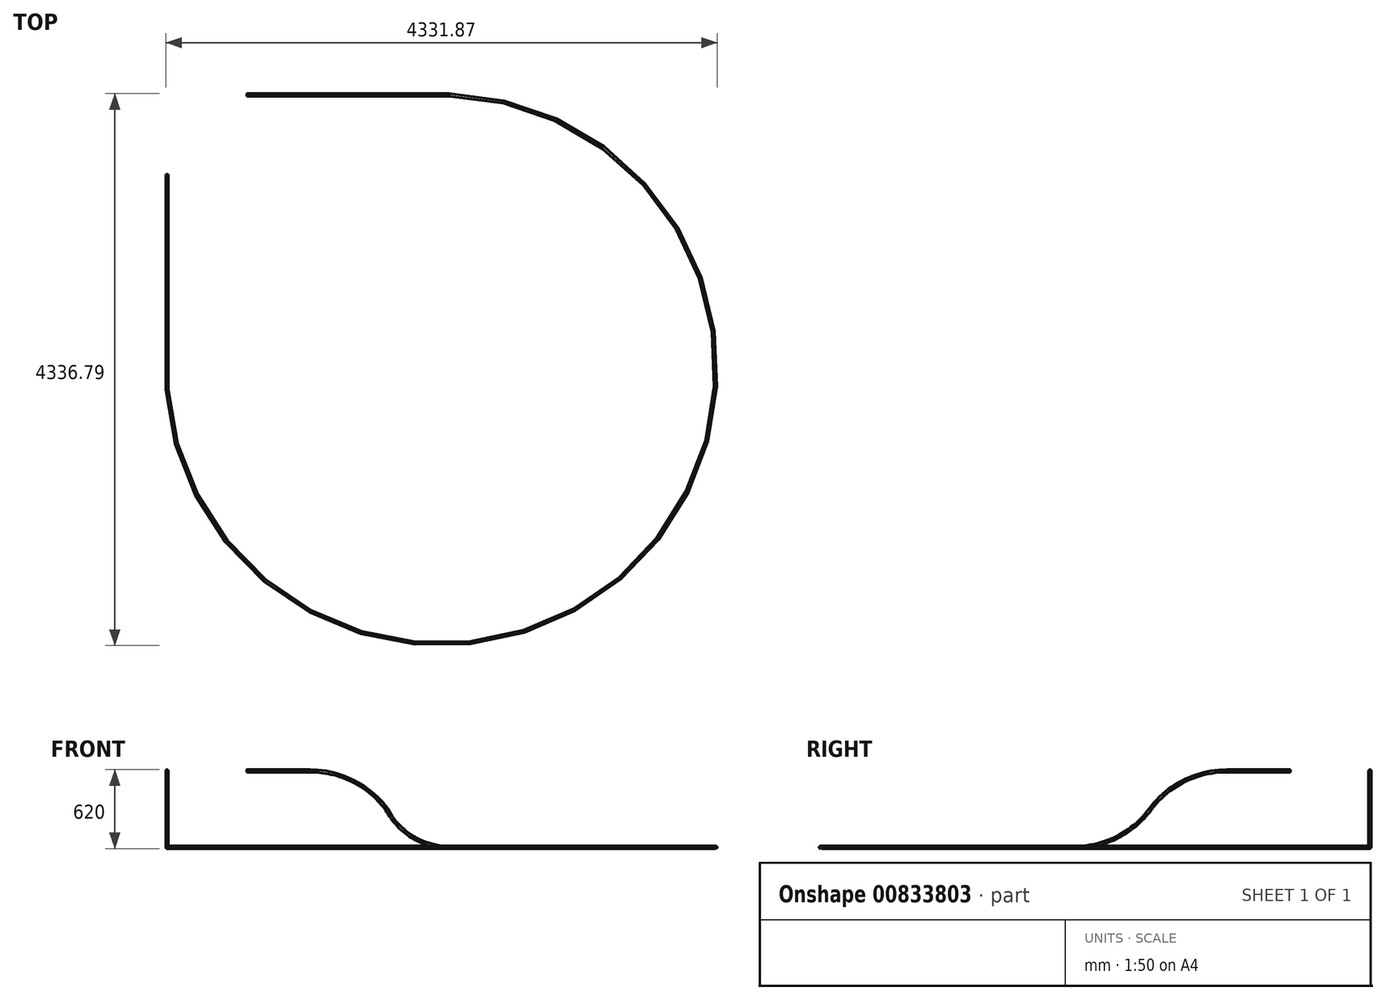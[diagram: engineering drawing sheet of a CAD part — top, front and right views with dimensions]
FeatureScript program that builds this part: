
annotation { "Feature Type Name" : "Feature", "Feature Type Description" : "" }
export const myFeature = defineFeature(function(context is Context, id is Id, definition is map)
    precondition{}
    {
        {
            var Q0;
            Q0=qCreatedBy(makeId("Top.planeOp"),FACE);
            var sketch = newSketch(context, id + "F0", { "sketchPlane" : qUnion([Q0])});
            skLineSegment(sketch, "E0", {"start": v(0, 0) * mm, "end": v(0, 1250) * mm});
            skLineSegment(sketch, "E1", {"start": v(0, 1250) * mm, "end": v(-1250, 1250) * mm});
            skLineSegment(sketch, "E2", {"start": v(-1250, 1250) * mm, "end": v(-1250, 0) * mm});
            skLineSegment(sketch, "E3", {"start": v(-1250, 0) * mm, "end": v(0, 0) * mm});
            skPoint(sketch, "E4", {"position": v(0, 625) * mm});
            skPoint(sketch, "E5", {"position": v(-625, 0) * mm});
            skSolve(sketch);
        }
        {
            var Q0;
            Q0=sQuery(id+"F0.wireOp",VERTEX,"E4");
            var Q1;
            Q1=sQuery(id+"F0.wireOp",EDGE,"E0");
            cPlane(context, id + "F1", {"entities" : qUnion([Q0, Q1]), "cplaneType" : CPlaneType.LINE_POINT, "offset" : 25 * mm, "width" : 150 * mm, "height" : 150 * mm});
        }
        {
            var Q0;
            Q0=qCreatedBy(id+"F1.planeOp",FACE);
            var sketch = newSketch(context, id + "F2", { "sketchPlane" : qUnion([Q0])});
            skLineSegment(sketch, "E6", {"start": v(0, 0) * mm, "end": v(-500, 0) * mm});
            skLineSegment(sketch, "E7", {"start": v(-500, 0) * mm, "end": v(-500, -300) * mm});
            skLineSegment(sketch, "E8", {"start": v(-500, -300) * mm, "end": v(-1100, -300) * mm});
            skArc(sketch, "E9", {"start": v(-500, 0) * mm, "mid": v(-835.41, -79.18) * mm, "end": v(-1100, -300) * mm});
            skLineSegment(sketch, "E10", {"start": v(-1100, -300) * mm, "end": v(-1100, -600) * mm});
            skLineSegment(sketch, "E11", {"start": v(-1100, -600) * mm, "end": v(-1591.48, -600) * mm});
            skArc(sketch, "E12", {"start": v(-1591.48, -600) * mm, "mid": v(-1303.57, -519.07) * mm, "end": v(-1100, -300) * mm});
            skLineSegment(sketch, "E13", {"start": v(-1591.48, -600) * mm, "end": v(-1591.48, -479.86) * mm});
            skSolve(sketch);
        }
        {
            var Q0;
            Q0=sQuery(id+"F0.wireOp",EDGE,"E3");
            cPoint(context, id + "F3", {"entities" : qUnion([Q0]), "parameter" : 0.5});
        }
        {
            var Q0;
            Q0 = qCreatedBy(id + "F3" ,VERTEX);
            var Q1;
            Q1=sQuery(id+"F0.wireOp",EDGE,"E3");
            cPlane(context, id + "F4", {"entities" : qUnion([Q0, Q1]), "cplaneType" : CPlaneType.LINE_POINT, "offset" : 25 * mm, "width" : 150 * mm, "height" : 150 * mm});
        }
        {
            var Q0;
            Q0=qCreatedBy(id+"F4.planeOp",FACE);
            var sketch = newSketch(context, id + "F5", { "sketchPlane" : qUnion([Q0])});
            skLineSegment(sketch, "E14", {"start": v(0, 0) * mm, "end": v(-500, 0) * mm});
            skLineSegment(sketch, "E15", {"start": v(-500, 0) * mm, "end": v(-500, -300) * mm});
            skLineSegment(sketch, "E16", {"start": v(-500, -300) * mm, "end": v(-1100, -300) * mm});
            skLineSegment(sketch, "E17", {"start": v(-1100, -300) * mm, "end": v(-1100, -600) * mm});
            skLineSegment(sketch, "E18", {"start": v(-1100, -600) * mm, "end": v(-1691.38, -600) * mm});
            skArc(sketch, "E19", {"start": v(-500, 0) * mm, "mid": v(-835.41, -79.18) * mm, "end": v(-1100, -300) * mm});
            skArc(sketch, "E20", {"start": v(-1691.38, -600) * mm, "mid": v(-1359.82, -520.71) * mm, "end": v(-1100, -300) * mm});
            skSolve(sketch);
        }
        {
            var Q0;
            Q0=sQuery(id+"F2.wireOp",VERTEX,"E11.end");
            var Q1;
            Q1=sQuery(id+"F2.wireOp",EDGE,"E13");
            cPlane(context, id + "F6", {"entities" : qUnion([Q0, Q1]), "cplaneType" : CPlaneType.LINE_POINT, "offset" : 25 * mm, "width" : 150 * mm, "height" : 150 * mm});
        }
        {
            var Q0;
            Q0=qCreatedBy(id+"F6.planeOp",FACE);
            var sketch = newSketch(context, id + "F7", { "sketchPlane" : qUnion([Q0])});
            skArc(sketch, "E21", {"start": v(-624.99, -1691.37) * mm, "mid": v(3087.67, -3025.27) * mm, "end": v(1591.48, 625) * mm});
            skSolve(sketch);
        }
        {
            var Q0;
            Q0=sQuery(id+"F0.wireOp",EDGE,"E0");
            cPoint(context, id + "F8", {"entities" : qUnion([Q0]), "parameter" : 0.5});
        }
        {
            var Q0;
            Q0 = qCreatedBy(id + "F8" ,VERTEX);
            var Q1;
            Q1=sQuery(id+"F2.wireOp",EDGE,"E6");
            cPlane(context, id + "F9", {"entities" : qUnion([Q0, Q1]), "cplaneType" : CPlaneType.LINE_POINT, "offset" : 25 * mm, "width" : 150 * mm, "height" : 150 * mm});
        }
        {
            var Q0;
            Q0=sQuery(id+"F0.wireOp",VERTEX,"E5");
            var Q1;
            Q1=sQuery(id+"F5.wireOp",EDGE,"E14");
            cPlane(context, id + "F10", {"entities" : qUnion([Q0, Q1]), "cplaneType" : CPlaneType.LINE_POINT, "offset" : 25 * mm, "width" : 150 * mm, "height" : 150 * mm});
        }
        {
            var Q0;
            Q0=qCreatedBy(id+"F10.planeOp",FACE);
            var sketch = newSketch(context, id + "F11", { "sketchPlane" : qUnion([Q0])});
            skCircle(sketch, "E22", {"center": v(-625.03, 0) * mm, "radius": 10 * mm});
            skSolve(sketch);
        }
        {
            var Q0;
            Q0=qCreatedBy(id+"F9.planeOp",FACE);
            var sketch = newSketch(context, id + "F12", { "sketchPlane" : qUnion([Q0])});
            skCircle(sketch, "E23", {"center": v(625.11, 0) * mm, "radius": 10 * mm});
            skSolve(sketch);
        }
        {
            var Q0;
            Q0=makeQuery(id+"F12.imprint","IMPRINT",FACE,{"disambiguationData":[TD([[makeQuery(id+"F12.imprint","IMPRINT",EDGE,{"derivedFrom":sQuery(id+"F12.wireOp",EDGE,"E23")}),1.0]])]});
            var Q1;
            Q1=sQuery(id+"F2.wireOp",EDGE,"E6");
            var Q2;
            Q2=sQuery(id+"F2.wireOp",EDGE,"E9");
            var Q3;
            Q3=sQuery(id+"F2.wireOp",EDGE,"E12");
            var Q4;
            Q4=sQuery(id+"F7.wireOp",EDGE,"E21");
            sweep(context, id + "F13", {"profiles" : qUnion([Q0]), "path" : qUnion([Q1, Q2, Q3, Q4])});
        }
        {
            var Q0;
            Q0=makeQuery(id+"F11.imprint","IMPRINT",FACE,{"disambiguationData":[TD([[makeQuery(id+"F11.imprint","IMPRINT",EDGE,{"derivedFrom":sQuery(id+"F11.wireOp",EDGE,"E22")}),1.0]])]});
            var Q1;
            Q1=sQuery(id+"F5.wireOp",EDGE,"E14");
            var Q2;
            Q2=sQuery(id+"F5.wireOp",EDGE,"E19");
            var Q3;
            Q3=sQuery(id+"F5.wireOp",EDGE,"E20");
            sweep(context, id + "F14", {"operationType" : NewBodyOperationType.ADD, "profiles" : qUnion([Q0]), "path" : qUnion([Q1, Q2, Q3])});
        }
    });
